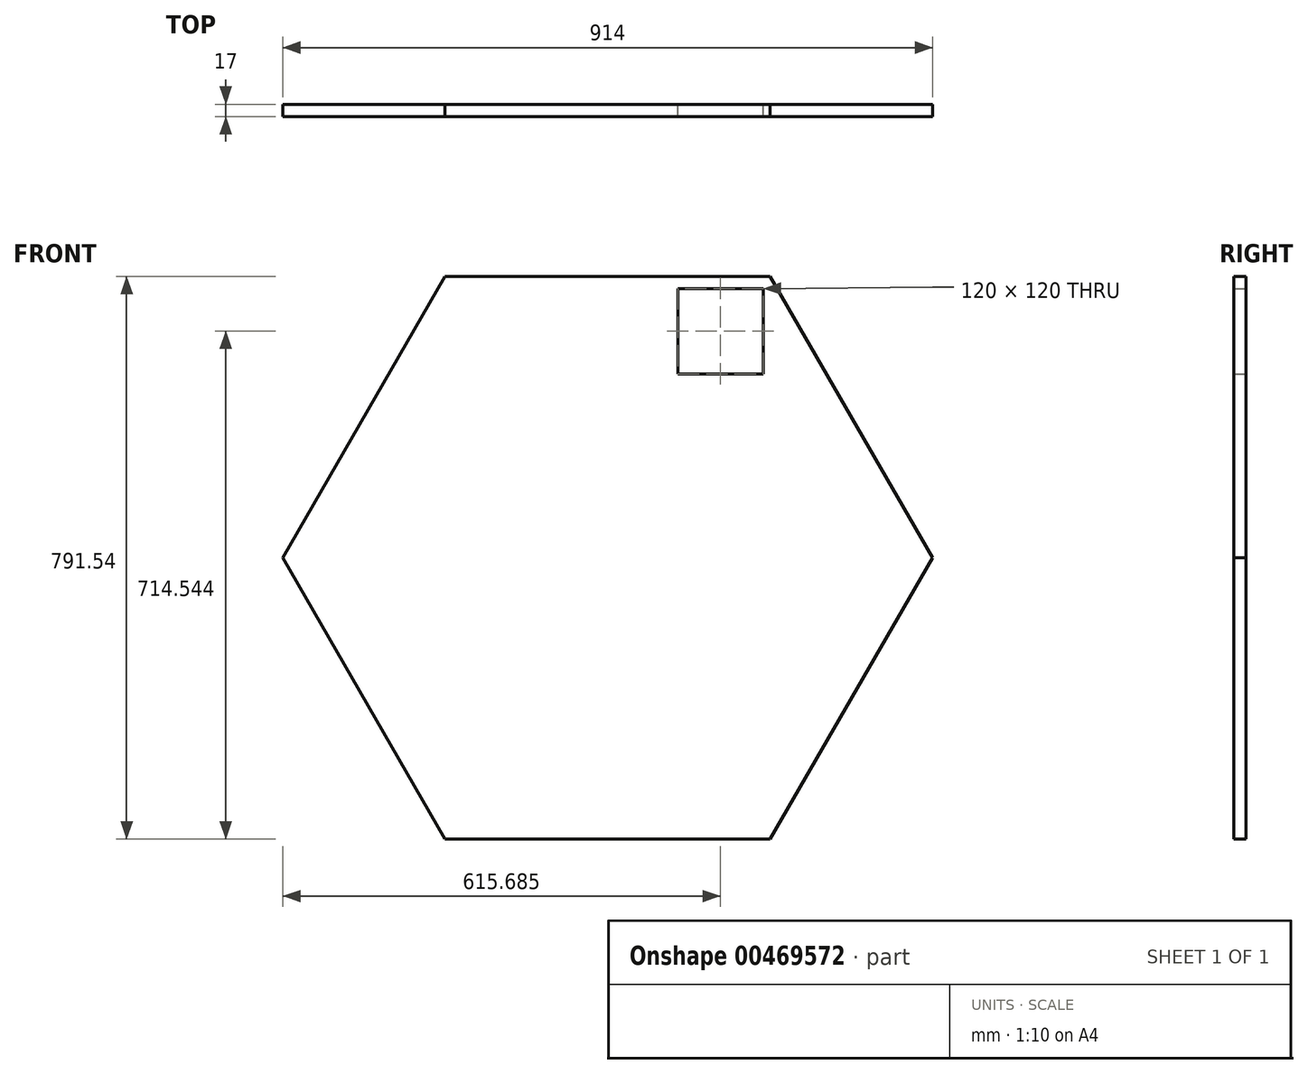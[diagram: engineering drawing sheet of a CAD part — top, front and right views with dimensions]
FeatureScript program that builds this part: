
annotation { "Feature Type Name" : "Feature", "Feature Type Description" : "" }
export const myFeature = defineFeature(function(context is Context, id is Id, definition is map)
    precondition{}
    {
        {
            var Q0;
            Q0=qCreatedBy(makeId("Front.planeOp"),FACE);
            var sketch = newSketch(context, id + "F0", { "sketchPlane" : qUnion([Q0])});
            skCircle(sketch, "E0.cCircle", {"center": v(0, 0) * mm, "radius": 395.77 * mm, "construction": true});
            skLineSegment(sketch, "E0.0", {"start": v(228.5, -395.77) * mm, "end": v(-228.5, -395.77) * mm});
            skLineSegment(sketch, "E0.1", {"start": v(-228.5, -395.77) * mm, "end": v(-457, 0) * mm});
            skLineSegment(sketch, "E0.2", {"start": v(-457, 0) * mm, "end": v(-228.5, 395.77) * mm});
            skLineSegment(sketch, "E0.3", {"start": v(-228.5, 395.77) * mm, "end": v(228.5, 395.77) * mm});
            skLineSegment(sketch, "E0.4", {"start": v(228.5, 395.77) * mm, "end": v(457, 0) * mm});
            skLineSegment(sketch, "E0.5", {"start": v(457, 0) * mm, "end": v(228.5, -395.77) * mm});
            skPoint(sketch, "E0.0.midPoint", {"position": v(0, -395.77) * mm});
            skSolve(sketch);
        }
        {
            var Q0;
            Q0 = qSketchRegion(id + "F0", true);
            extrude(context, id + "F1", {"entities" : qUnion([Q0]), "depth" : 17 * mm});
        }
        {
            var Q0;
            Q0=makeQuery(id+"F1.opExtrude","CAP_FACE",FACE,{"disambiguationData":[OSD([sQuery(id+"F0.wireOp",EDGE,"E0.0"),sQuery(id+"F0.wireOp",EDGE,"E0.1"),sQuery(id+"F0.wireOp",EDGE,"E0.2"),sQuery(id+"F0.wireOp",EDGE,"E0.3"),sQuery(id+"F0.wireOp",EDGE,"E0.4"),sQuery(id+"F0.wireOp",EDGE,"E0.5")])],"isStart":true});
            var sketch = newSketch(context, id + "F2", { "sketchPlane" : qUnion([Q0])});
            skLineSegment(sketch, "E1.bottom", {"start": v(-218.69, 378.77) * mm, "end": v(-98.69, 378.77) * mm});
            skLineSegment(sketch, "E1.top", {"start": v(-218.69, 258.77) * mm, "end": v(-98.69, 258.77) * mm});
            skLineSegment(sketch, "E1.left", {"start": v(-218.69, 378.77) * mm, "end": v(-218.69, 258.77) * mm});
            skLineSegment(sketch, "E1.right", {"start": v(-98.69, 378.77) * mm, "end": v(-98.69, 258.77) * mm});
            skSolve(sketch);
        }
        {
            var Q0;
            Q0 = qSketchRegion(id + "F2", true);
            extrude(context, id + "F3", {"entities" : qUnion([Q0]), "operationType" : NewBodyOperationType.REMOVE, "oppositeDirection" : true, "depth" : 17 * mm});
        }
    });
